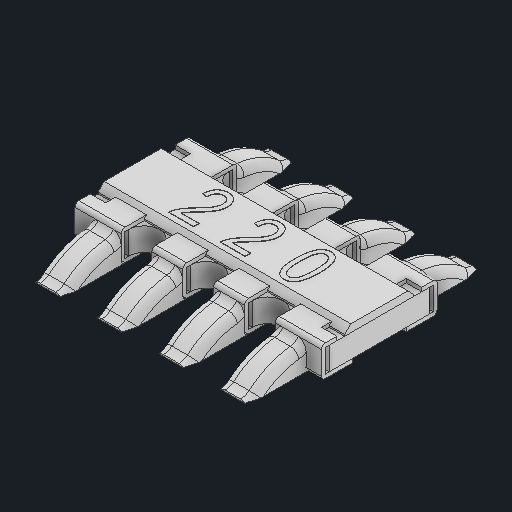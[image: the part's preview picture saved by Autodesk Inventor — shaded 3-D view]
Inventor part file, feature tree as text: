
AUTODESK INVENTOR PART (.ipt)
format: ipt  version: 2023 (Build 270158000, 158)  size: 518,656 bytes
history: native  units: in
note: dims shown in document units (in); Inventor stores cm internally (conversion verified against a paired STEP export)
features: other x8, fillet x2
ambient origin geometry x8: Origin, YZ Plane, XZ Plane, XY Plane, X Axis, Y Axis, Z Axis, Center Point
bodies: Solid1 (feature_tree), Solid2 (feature_tree), Solid3 (feature_tree), Solid4 (feature_tree), Solid5 (feature_tree), Solid6 (feature_tree), Solid7 (feature_tree), Solid8 (feature_tree), Solid9 (feature_tree), Solid10 (feature_tree)
feature tree (10):
  other  "Cut-Extrude7"
  other  "Boss-Extrude5"
  fillet  "Fillet2"  [1 undecoded]
  fillet  "Fillet1"  [1 undecoded]
  other  "LPattern3[1]"
  other  "LPattern3[2]"
  other  "LPattern3[3]"
  other  "LPattern3[4]"
  other  "LPattern3[5]"
  other  "LPattern3[6]"
note: 2 required parameter values undecoded (feature->parameter linkage not recoverable at this tier; creation-order binding heuristic only, values carry confidence <= 0.55)
